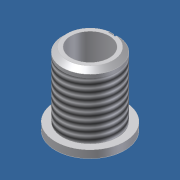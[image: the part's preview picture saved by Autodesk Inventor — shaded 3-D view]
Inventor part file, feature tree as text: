
AUTODESK INVENTOR PART (.ipt)
format: ipt  version: 2014 (Build 180170000, 170)  size: 145,408 bytes
history: native  units: in
note: dims shown in document units (in); Inventor stores cm internally (conversion verified against a paired STEP export)
features: other x35, sketch x5, extrude x3, revolve x2, thread x1
ambient origin geometry x8: Origin, YZ Plane, XZ Plane, XY Plane, X Axis, Y Axis, Z Axis, Center Point
bodies: Solid1 (feature_tree)
feature tree (46):
  extrude  "Extrusion1"  TaperAngle=360.0deg  [1 undecoded]
  revolve  "Revolution1"  [1 undecoded]
  thread  "Thread1"  [1 undecoded]
  extrude  "Extrusion2"  [1 undecoded]
  revolve  "Revolution2"  [1 undecoded]
  extrude  "Extrusion3"  [1 undecoded]
  other  "1_XY"
  other  "1_YZ"
  other  "1_ZX"
  other  "1_X"
  other  "1_Y"
  other  "1_Z"
  other  "1_Center"
  other  "2_XY"
  other  "2_YZ"
  other  "2_ZX"
  other  "2_X"
  other  "2_Y"
  other  "2_Z"
  other  "2_Center"
  other  "3_XY"
  other  "3_YZ"
  other  "3_ZX"
  other  "3_X"
  other  "3_Y"
  other  "3_Z"
  other  "3_Center"
  other  "4_XY"
  other  "4_YZ"
  other  "4_ZX"
  other  "4_X"
  other  "4_Y"
  other  "4_Z"
  other  "4_Center"
  other  "to_base_XY"
  other  "to_base_YZ"
  other  "to_base_ZX"
  other  "to_base_X"
  other  "to_base_Y"
  other  "to_base_Z"
  other  "to_base_Center"
  sketch  "Sketch_1"  dims[d0=0.512in d1=0.0in d2=360.0deg]
  sketch  "Sketch_6"
  sketch  "Sketch_8"
  sketch  "Sketch_10_ALT_Drilling_1"  dims[d3=0.2593in d4=0.0157in d5=0.385in d6=0.0in d7=360.0deg]
  sketch  "Sketch_2"  dims[d8=0.512in d9=0.0in]
note: 6 required parameter values undecoded (feature->parameter linkage not recoverable at this tier; creation-order binding heuristic only, values carry confidence <= 0.55)